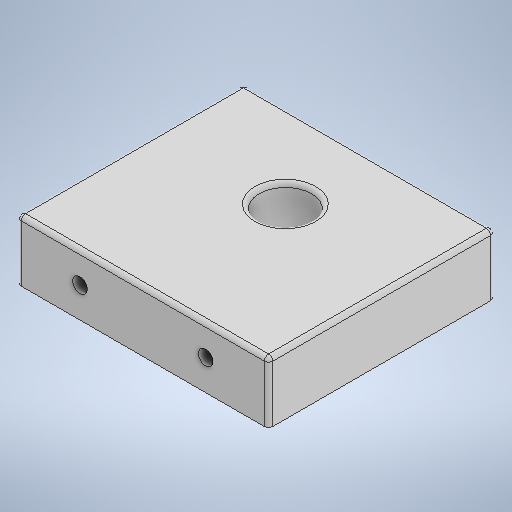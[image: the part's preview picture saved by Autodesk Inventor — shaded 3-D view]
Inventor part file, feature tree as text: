
AUTODESK INVENTOR PART (.ipt)
format: ipt  version: 2025.1 (Build 291241000, 241)  size: 294,400 bytes
history: native  units: mm
features: extrude x2, sketch x2, fillet x1
ambient origin geometry x8: Origin, YZ Plane, XZ Plane, XY Plane, X Axis, Y Axis, Z Axis, Center Point
bodies: Solide1 (feature_tree)
feature tree (5):
  extrude  "Extrusion1"  Depth=54.0mm
  sketch  "Esquisse2"
  fillet  "Congé1"  Radius=60.0mm
  extrude  "Extrusion2"  Depth=34.0mm
  sketch  "Esquisse1"
